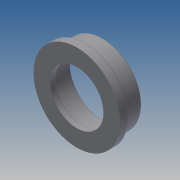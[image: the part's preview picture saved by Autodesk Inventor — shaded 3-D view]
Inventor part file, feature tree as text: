
AUTODESK INVENTOR PART (.ipt)
format: ipt  version: 2014 (Build 180170000, 170)  size: 138,752 bytes
history: native  units: mm
features: revolve x1, fillet x1, sketch x1
ambient origin geometry x8: Origin, YZ Plane, XZ Plane, XY Plane, X Axis, Y Axis, Z Axis, Center Point
bodies: Solid1 (feature_tree)
feature tree (3):
  revolve  "Revolution1"  [1 undecoded]
  fillet  "Fillet1"  Radius=13.26mm
  sketch  "Sketch1"  dims[d0=2.0mm d1=7.0mm d2=13.26mm d3=14.875mm d4=6.0mm d5=11.1mm d6=2.0mm d7=90.0deg d8=0.5mm]
note: 1 required parameter value undecoded (feature->parameter linkage not recoverable at this tier; creation-order binding heuristic only, values carry confidence <= 0.55)
